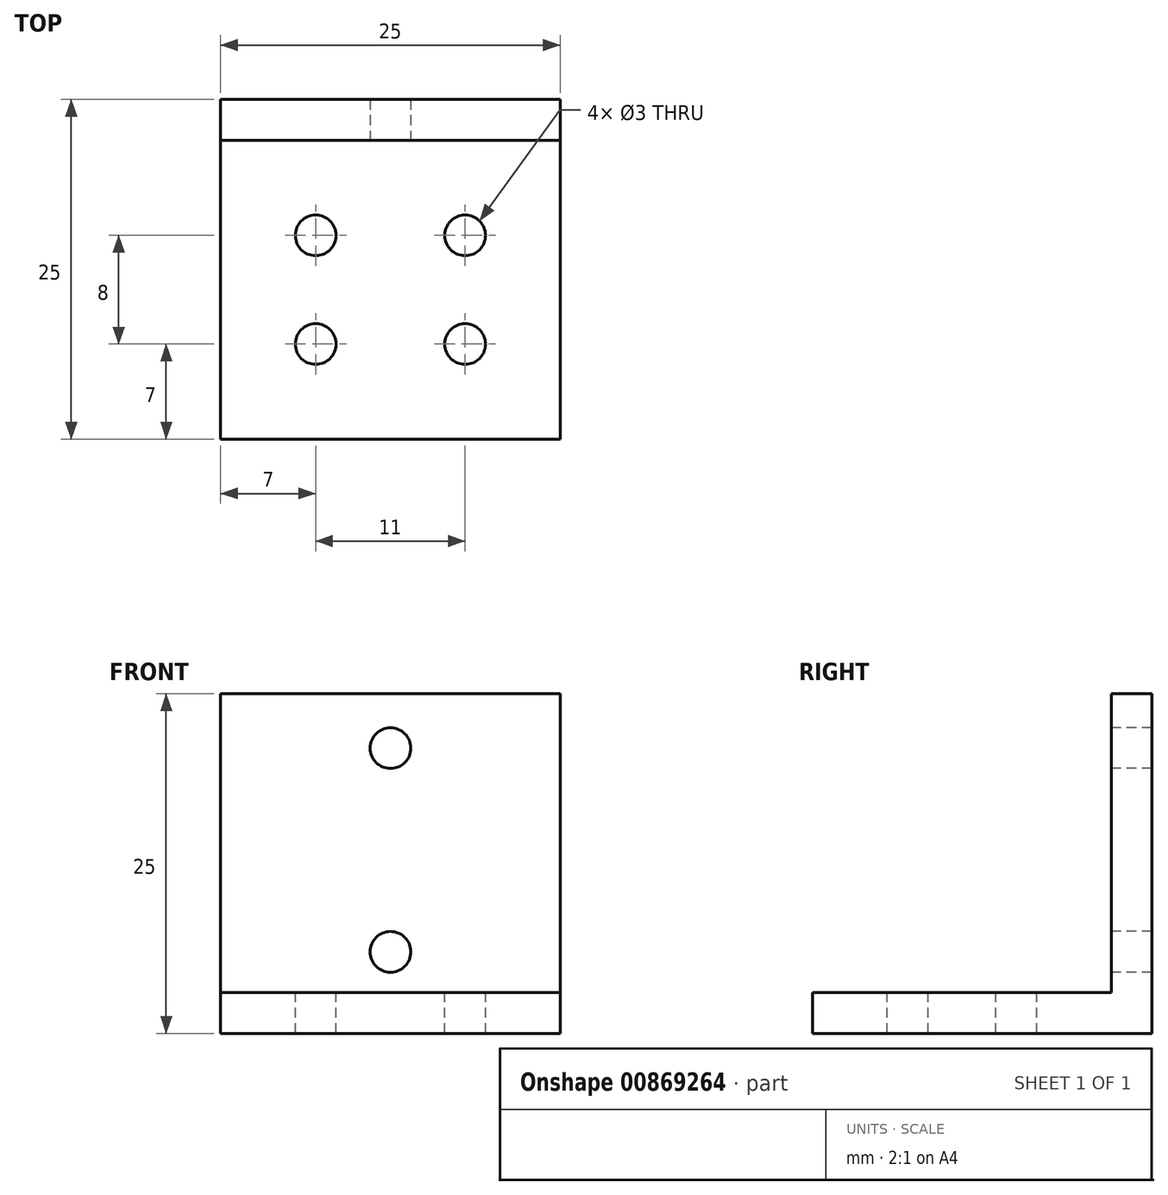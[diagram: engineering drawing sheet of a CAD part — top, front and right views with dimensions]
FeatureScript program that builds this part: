
annotation { "Feature Type Name" : "Feature", "Feature Type Description" : "" }
export const myFeature = defineFeature(function(context is Context, id is Id, definition is map)
    precondition{}
    {
        {
            var Q0;
            Q0=qCreatedBy(makeId("Top.planeOp"),FACE);
            var sketch = newSketch(context, id + "F0", { "sketchPlane" : qUnion([Q0])});
            skLineSegment(sketch, "E0.bottom", {"start": v(12.5, -12.5) * mm, "end": v(-12.5, -12.5) * mm});
            skLineSegment(sketch, "E0.top", {"start": v(12.5, 12.5) * mm, "end": v(-12.5, 12.5) * mm});
            skLineSegment(sketch, "E0.left", {"start": v(12.5, -12.5) * mm, "end": v(12.5, 12.5) * mm});
            skLineSegment(sketch, "E0.right", {"start": v(-12.5, -12.5) * mm, "end": v(-12.5, 12.5) * mm});
            skPoint(sketch, "E0.middle", {"position": v(0, 0) * mm});
            skSolve(sketch);
        }
        {
            var Q0;
            Q0=makeQuery(id+"F0.imprint","IMPRINT",FACE,{"disambiguationData":[TD([[makeQuery(id+"F0.imprint","IMPRINT",EDGE,{"derivedFrom":sQuery(id+"F0.wireOp",EDGE,"E0.bottom")}),-1.0]])]});
            extrude(context, id + "F1", {"entities" : qUnion([Q0]), "depth" : 3 * mm, "offsetDistance" : 25 * mm});
        }
        {
            var Q0;
            Q0=makeQuery(id+"F1.opExtrude","CAP_FACE",FACE,{"disambiguationData":[OSD([sQuery(id+"F0.wireOp",EDGE,"E0.bottom"),sQuery(id+"F0.wireOp",EDGE,"E0.top"),sQuery(id+"F0.wireOp",EDGE,"E0.left"),sQuery(id+"F0.wireOp",EDGE,"E0.right")])],"isStart":false});
            var sketch = newSketch(context, id + "F2", { "sketchPlane" : qUnion([Q0])});
            skLineSegment(sketch, "E1", {"start": v(5.5, -12.5) * mm, "end": v(5.5, -5.5) * mm});
            skLineSegment(sketch, "E2", {"start": v(5.5, -5.5) * mm, "end": v(12.5, -5.5) * mm});
            skLineSegment(sketch, "E3", {"start": v(-12.5, 2.5) * mm, "end": v(-5.5, 2.5) * mm});
            skLineSegment(sketch, "E4", {"start": v(-5.5, 2.5) * mm, "end": v(-5.5, 12.5) * mm});
            skLineSegment(sketch, "E5.bottom", {"start": v(12.5, 12.5) * mm, "end": v(5.5, 12.5) * mm});
            skLineSegment(sketch, "E5.top", {"start": v(12.5, 2.5) * mm, "end": v(5.5, 2.5) * mm});
            skLineSegment(sketch, "E5.left", {"start": v(12.5, 12.5) * mm, "end": v(12.5, 2.5) * mm});
            skLineSegment(sketch, "E5.right", {"start": v(5.5, 12.5) * mm, "end": v(5.5, 2.5) * mm});
            skLineSegment(sketch, "E6.bottom", {"start": v(-12.5, -12.5) * mm, "end": v(-5.5, -12.5) * mm});
            skLineSegment(sketch, "E6.top", {"start": v(-12.5, -5.5) * mm, "end": v(-5.5, -5.5) * mm});
            skLineSegment(sketch, "E6.left", {"start": v(-12.5, -12.5) * mm, "end": v(-12.5, -5.5) * mm});
            skLineSegment(sketch, "E6.right", {"start": v(-5.5, -12.5) * mm, "end": v(-5.5, -5.5) * mm});
            skSolve(sketch);
        }
        {
            var Q0;
            Q0=sQuery(id+"F2.wireOp",VERTEX,"E5.top.end");
            var Q1;
            Q1=sQuery(id+"F2.wireOp",VERTEX,"E1.end");
            var Q2;
            Q2=sQuery(id+"F2.wireOp",VERTEX,"E6.top.end");
            var Q3;
            Q3=sQuery(id+"F2.wireOp",VERTEX,"E3.end");
            var Q4;
            Q4=makeQuery(id+"F1.opExtrude","SWEPT_BODY",BODY,{"disambiguationData":[OSD([sQuery(id+"F0.wireOp",EDGE,"E0.bottom"),sQuery(id+"F0.wireOp",EDGE,"E0.top"),sQuery(id+"F0.wireOp",EDGE,"E0.left"),sQuery(id+"F0.wireOp",EDGE,"E0.right")])]});
            hole(context, id + "F3", {"style" : HoleStyle.SIMPLE, "endStyle" : HoleEndStyle.BLIND, "holeDiameter" : 3 * mm, "majorDiameter" : 5 * mm, "holeDepth" : 15 * mm, "isTappedThrough" : true, "tappedDepth" : 12 * mm, "tapClearance" : 3, "locations" : qUnion([Q0, Q1, Q2, Q3]), "scope" : qUnion([Q4])});
        }
        {
            var Q0;
            Q0=makeQuery(id+"F1.opExtrude","CAP_FACE",FACE,{"disambiguationData":[OSD([sQuery(id+"F0.wireOp",EDGE,"E0.bottom"),sQuery(id+"F0.wireOp",EDGE,"E0.top"),sQuery(id+"F0.wireOp",EDGE,"E0.left"),sQuery(id+"F0.wireOp",EDGE,"E0.right")])],"isStart":false});
            var sketch = newSketch(context, id + "F4", { "sketchPlane" : qUnion([Q0])});
            skLineSegment(sketch, "E7.bottom", {"start": v(-12.5, 12.5) * mm, "end": v(12.5, 12.5) * mm});
            skLineSegment(sketch, "E7.top", {"start": v(-12.5, 9.5) * mm, "end": v(12.5, 9.5) * mm});
            skLineSegment(sketch, "E7.left", {"start": v(-12.5, 12.5) * mm, "end": v(-12.5, 9.5) * mm});
            skLineSegment(sketch, "E7.right", {"start": v(12.5, 12.5) * mm, "end": v(12.5, 9.5) * mm});
            skSolve(sketch);
        }
        {
            var Q0;
            Q0=makeQuery(id+"F4.imprint","IMPRINT",FACE,{"disambiguationData":[TD([[makeQuery(id+"F4.imprint","IMPRINT",EDGE,{"derivedFrom":sQuery(id+"F4.wireOp",EDGE,"E7.bottom")}),1.0]])]});
            extrude(context, id + "F5", {"entities" : qUnion([Q0]), "operationType" : NewBodyOperationType.ADD, "depth" : 22 * mm, "offsetDistance" : 25 * mm});
        }
        {
            var Q0;
            Q0=makeQuery(id+"F5.opExtrude","SWEPT_FACE",FACE,{"disambiguationData":[OSD([sQuery(id+"F4.wireOp",EDGE,"E7.top")])]});
            var sketch = newSketch(context, id + "F6", { "sketchPlane" : qUnion([Q0])});
            skLineSegment(sketch, "E8", {"start": v(0, 25) * mm, "end": v(0, 21) * mm});
            skLineSegment(sketch, "E9", {"start": v(0, 21) * mm, "end": v(0, 6) * mm});
            skLineSegment(sketch, "E10", {"start": v(0, 6) * mm, "end": v(0, 3) * mm});
            skSolve(sketch);
        }
        {
            var Q0;
            Q0=sQuery(id+"F6.wireOp",VERTEX,"E8.end");
            var Q1;
            Q1=sQuery(id+"F6.wireOp",VERTEX,"E9.end");
            var Q2;
            Q2=makeQuery(id+"F1.opExtrude","SWEPT_BODY",BODY,{"disambiguationData":[OSD([sQuery(id+"F0.wireOp",EDGE,"E0.bottom"),sQuery(id+"F0.wireOp",EDGE,"E0.top"),sQuery(id+"F0.wireOp",EDGE,"E0.left"),sQuery(id+"F0.wireOp",EDGE,"E0.right")])]});
            hole(context, id + "F7", {"style" : HoleStyle.SIMPLE, "endStyle" : HoleEndStyle.THROUGH, "holeDiameter" : 3 * mm, "majorDiameter" : 5 * mm, "isTappedThrough" : true, "tappedDepth" : 12 * mm, "tapClearance" : 3, "locations" : qUnion([Q0, Q1]), "scope" : qUnion([Q2])});
        }
    });
